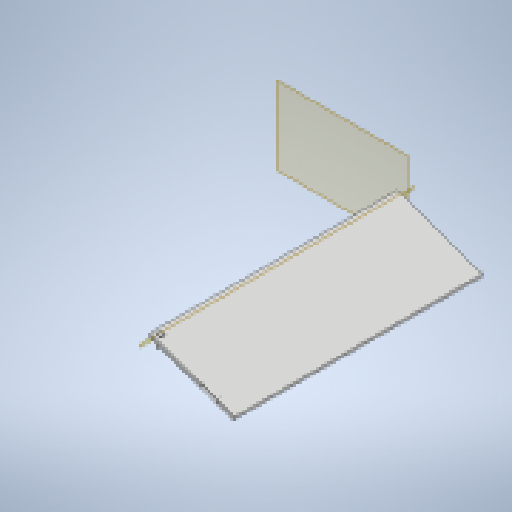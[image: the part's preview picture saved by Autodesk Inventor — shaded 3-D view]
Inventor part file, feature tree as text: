
AUTODESK INVENTOR PART (.ipt)
format: ipt  version: 2023 (Build 270158030, 158C)  size: 303,104 bytes
history: native  units: mm
features: other x8, extrude x4, sketch x4, reference x3, plane x2, fillet x1, pattern_linear x1
ambient origin geometry x8: Origin, YZ Plane, XZ Plane, XY Plane, X Axis, Y Axis, Z Axis, Center Point
bodies: Body1 (feature_tree), Body2 (feature_tree), Body3 (feature_tree)
feature tree (23):
  other  "bed-base"
  plane  "Work Plane4"
  extrude  "Extrusion1"  Depth=30.0mm
  extrude  "Extrusion2"  Depth=10.0mm
  extrude  "Extrusion3"  Depth=22.0mm
  fillet  "Fillet1"  Radius=4.0mm
  plane  "Work Plane5"
  extrude  "Extrusion4"  TaperAngle=0.0deg  [1 undecoded]
  pattern_linear  "Rectangular Pattern1"  Count1=3 Spacing1=0.0mm
  sketch  "Sketch3"  dims[d1=700.0mm d2=30.0mm]
  reference  "Reference2"
  sketch  "Sketch4"  dims[d3=5.0mm d4=10.0mm]
  reference  "Reference3"
  sketch  "Sketch5"  dims[d5=1930.0mm d6=0.0mm d7=22.0mm d8=4.0mm]
  other  "location-pin"
  sketch  "Sketch6"  dims[d9=4.0mm d11=0.0mm d12=30.0mm d13=0.0mm d14=20.0mm d15=15.0mm d16=15.0mm d17=90.0mm d18=25.0mm d19=0.0mm d20=6.0mm d21=120.0mm d22=-30.0mm d23=2.5mm d24=11.0mm d25=25.0mm d26=3.0mm d27=4.0mm d28=6.0mm d29=3.0mm d30=20.0mm d31=30.0mm d32=0.0mm d33=110.0mm d35=60.0mm]
  reference  "Reference4"
  other  "hinge"
  other  "<userpath>\Documents\0004-inventor\3D-CAD-main\primary-engineer-bench.iam"
  other  "primary-engineer-bench.iam"
  other  "bench-end-peice_MIR:1"
  other  "bench-end-peice:1"
  other  "back-flaps-3:1"
note: 1 required parameter value undecoded (feature->parameter linkage not recoverable at this tier; creation-order binding heuristic only, values carry confidence <= 0.55)
